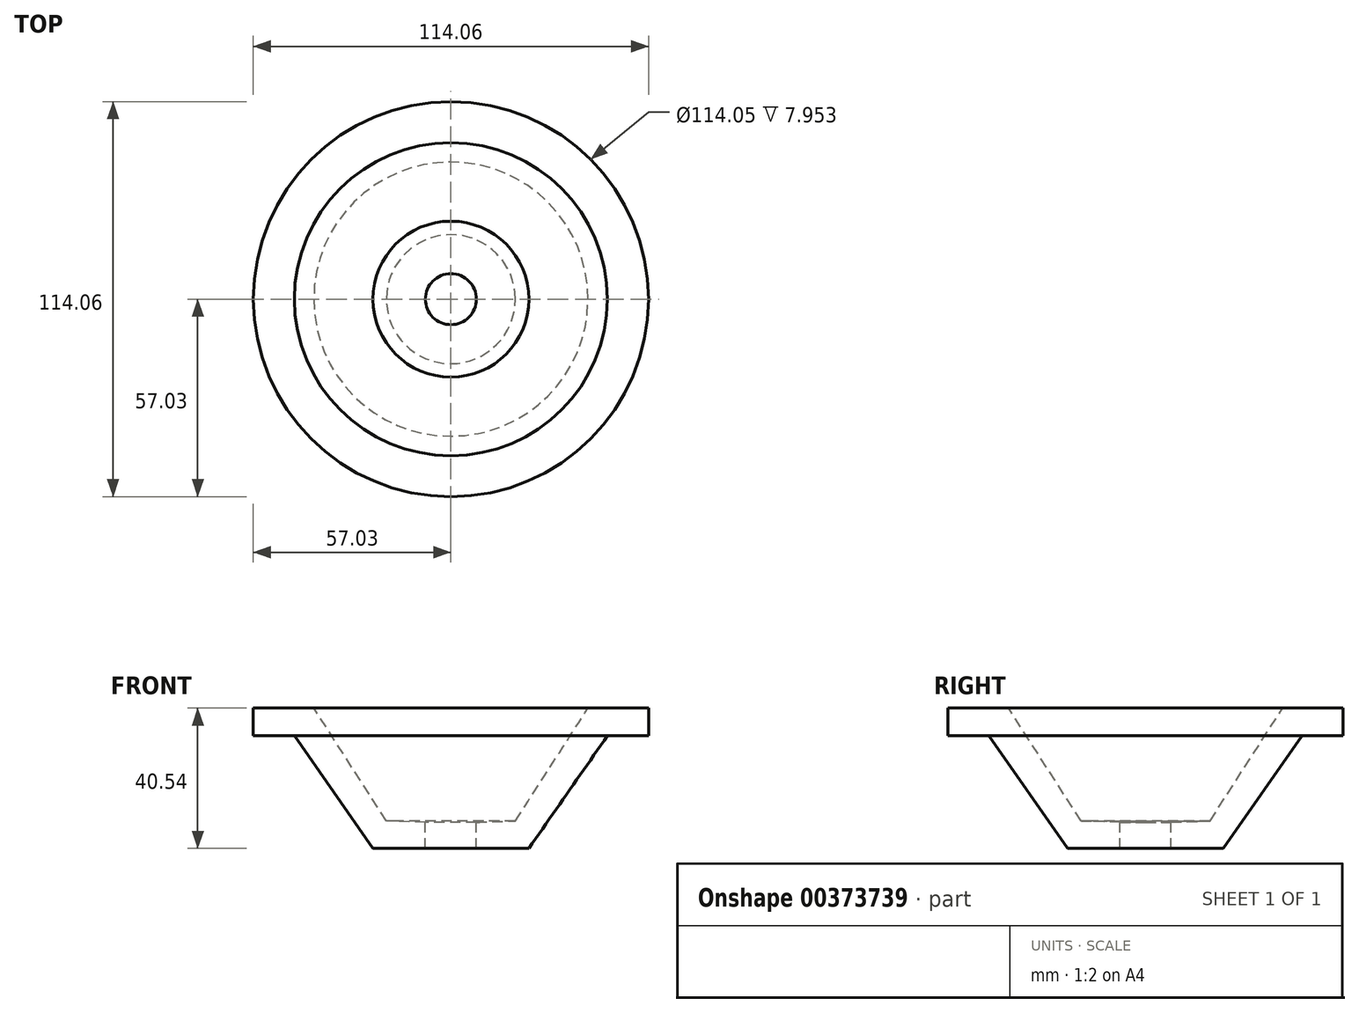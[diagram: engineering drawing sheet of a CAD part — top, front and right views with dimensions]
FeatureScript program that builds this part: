
annotation { "Feature Type Name" : "Feature", "Feature Type Description" : "" }
export const myFeature = defineFeature(function(context is Context, id is Id, definition is map)
    precondition{}
    {
        {
            var Q0;
            Q0=qCreatedBy(makeId("Front.planeOp"),FACE);
            var sketch = newSketch(context, id + "F0", { "sketchPlane" : qUnion([Q0])});
            skLineSegment(sketch, "E0", {"start": v(7.37, 7.56) * mm, "end": v(7.37, 0) * mm});
            skLineSegment(sketch, "E1", {"start": v(7.37, 0) * mm, "end": v(22.5, 0) * mm});
            skLineSegment(sketch, "E2", {"start": v(22.5, 0) * mm, "end": v(45.2, 32.59) * mm});
            skLineSegment(sketch, "E3", {"start": v(45.2, 32.59) * mm, "end": v(57.03, 32.59) * mm});
            skLineSegment(sketch, "E4", {"start": v(57.03, 32.59) * mm, "end": v(57.03, 40.54) * mm});
            skLineSegment(sketch, "E5", {"start": v(57.03, 40.54) * mm, "end": v(39.57, 40.54) * mm});
            skLineSegment(sketch, "E6", {"start": v(39.57, 40.54) * mm, "end": v(18.62, 7.95) * mm});
            skLineSegment(sketch, "E7", {"start": v(18.62, 7.95) * mm, "end": v(7.37, 7.56) * mm});
            skLineSegment(sketch, "E8", {"start": v(0, 0) * mm, "end": v(0, 43.25) * mm, "construction": true});
            skSolve(sketch);
        }
        {
            var Q0;
            Q0=sQuery(id+"F0.wireOp",EDGE,"E8");
            var Q1;
            Q1=sQuery(id+"F0.wireOp",EDGE,"E7");
            var Q2;
            Q2=sQuery(id+"F0.wireOp",EDGE,"E6");
            var Q3;
            Q3=sQuery(id+"F0.wireOp",EDGE,"E5");
            var Q4;
            Q4=sQuery(id+"F0.wireOp",EDGE,"E3");
            var Q5;
            Q5=sQuery(id+"F0.wireOp",EDGE,"E4");
            var Q6;
            Q6=sQuery(id+"F0.wireOp",EDGE,"E2");
            var Q7;
            Q7=sQuery(id+"F0.wireOp",EDGE,"E1");
            var Q8;
            Q8=sQuery(id+"F0.wireOp",EDGE,"E0");
            var Q9;
            Q9=sQuery(id+"F0.wireOp",EDGE,"E8");
            revolve(context, id + "F1", {"bodyType" : ToolBodyType.SURFACE, "surfaceEntities" : qUnion([Q0, Q1, Q2, Q3, Q4, Q5, Q6, Q7, Q8]), "axis" : qUnion([Q9]), "revolveType" : RevolveType.FULL});
        }
    });
